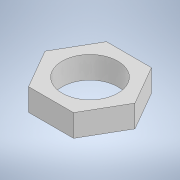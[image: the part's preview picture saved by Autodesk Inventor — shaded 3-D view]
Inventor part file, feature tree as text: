
AUTODESK INVENTOR PART (.ipt)
format: ipt  version: 2022 (Build 260153000, 153)  size: 104,960 bytes
history: native  units: in
note: dims shown in document units (in); Inventor stores cm internally (conversion verified against a paired STEP export)
features: extrude x2, sketch x2
ambient origin geometry x8: Origin, YZ Plane, XZ Plane, XY Plane, X Axis, Y Axis, Z Axis, Center Point
bodies: Solid1 (feature_tree)
feature tree (4):
  extrude  "Extrusion1"  Depth=0.0787in TaperAngle=0.0deg
  extrude  "Extrusion3"  Depth=0.3937in TaperAngle=0.0deg
  sketch  "Sketch1"  dims[d0=0.2756in d1=0.0787in d2=0.0in]
  sketch  "Sketch3"  dims[d6=0.1969in d7=0.3937in d8=0.0in]
